# Revit family: C_FP30_15_10_2DO_CAD_MULT_Prod
name_source: partatom
category: Detail Items
revit_build: Autodesk Revit 2015 (Build: 20140606_1530(x64)
units: mm (PartAtom-declared; Revit-internal decimal feet)

## types (2) — shared parameters
Density = 3.10 kg
Description = Straps
EPD = https://www.strongtie.eu
ETA / DoP = https://www.strongtie.eu
Manufacturer = Simpson Strong-Tie
Model = FP30/1.5/10
Model Disclaimer = Contact Simpson Strong-Tie Company  for more information
Model ID = 0310176357297750785783237889048433075607
Name = FP30/1.5/10
ObjectType = FP30/1.5/10
Product Material = Galvanised
Product Type = Straps
Reference = FP30/1.5/10
Technical datasheet = https://www.strongtie.eu
URL = www.strongtie.eu
UniClass Number = Pr_20_29_31_13
UniClass Title = Carbon steel punched metal plate fasteners

## per-type parameters (varying)
| type | _visiblefront | _visibleleft |
| SST_FP30/1.5/10_Front | Yes | No |
| SST_FP30/1.5/10_Left | No | Yes |

## geometry (parser evidence)
native form markers: Sweep x5
no freeform markers — native parametric forms only
